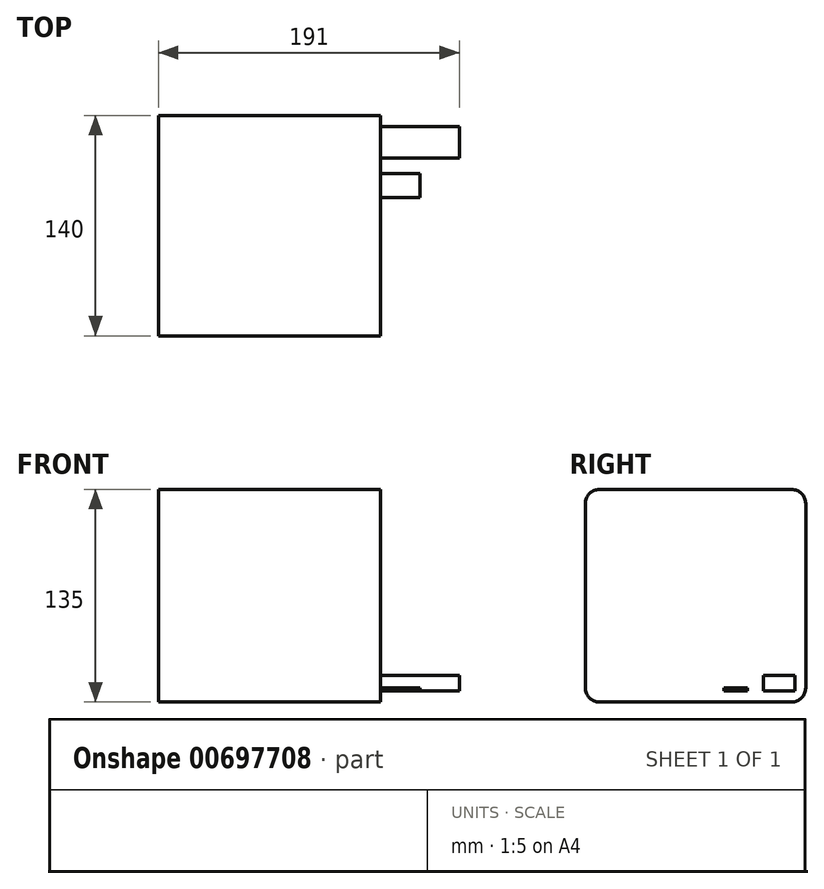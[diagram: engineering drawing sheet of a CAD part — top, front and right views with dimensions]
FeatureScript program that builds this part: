
annotation { "Feature Type Name" : "Feature", "Feature Type Description" : "" }
export const myFeature = defineFeature(function(context is Context, id is Id, definition is map)
    precondition{}
    {
        {
            var Q0;
            Q0=qCreatedBy(makeId("Top.planeOp"),FACE);
            var sketch = newSketch(context, id + "F0", { "sketchPlane" : qUnion([Q0])});
            skLineSegment(sketch, "E0.bottom", {"start": v(0, 0) * mm, "end": v(141, 0) * mm});
            skLineSegment(sketch, "E0.top", {"start": v(0, 140) * mm, "end": v(141, 140) * mm});
            skLineSegment(sketch, "E0.left", {"start": v(0, 0) * mm, "end": v(0, 140) * mm});
            skLineSegment(sketch, "E0.right", {"start": v(141, 0) * mm, "end": v(141, 140) * mm});
            skSolve(sketch);
        }
        {
            var Q0;
            Q0=makeQuery(id+"F0.imprint","IMPRINT",FACE,{"disambiguationData":[TD([[makeQuery(id+"F0.imprint","IMPRINT",EDGE,{"derivedFrom":sQuery(id+"F0.wireOp",EDGE,"E0.bottom")}),1.0]])]});
            extrude(context, id + "F1", {"entities" : qUnion([Q0]), "depth" : 135 * mm, "offsetDistance" : 25 * mm});
        }
        {
            var Q0;
            Q0=makeQuery(id+"F1.opExtrude","SWEPT_FACE",FACE,{"disambiguationData":[OSD([sQuery(id+"F0.wireOp",EDGE,"E0.right")])]});
            var sketch = newSketch(context, id + "F2", { "sketchPlane" : qUnion([Q0])});
            skLineSegment(sketch, "E1", {"start": v(140, 140) * mm, "end": v(140, 0) * mm});
            skLineSegment(sketch, "E2", {"start": v(0, 135) * mm, "end": v(150, 135) * mm});
            skLineSegment(sketch, "E3", {"start": v(0, 140) * mm, "end": v(0, 0) * mm});
            skLineSegment(sketch, "E4", {"start": v(0, 0) * mm, "end": v(150, 0) * mm});
            skLineSegment(sketch, "E5.bottom", {"start": v(103, 9) * mm, "end": v(88, 9) * mm});
            skLineSegment(sketch, "E5.top", {"start": v(103, 7) * mm, "end": v(88, 7) * mm});
            skLineSegment(sketch, "E5.left", {"start": v(103, 9) * mm, "end": v(103, 7) * mm});
            skLineSegment(sketch, "E5.right", {"start": v(88, 9) * mm, "end": v(88, 7) * mm});
            skLineSegment(sketch, "E6.bottom", {"start": v(133, 17) * mm, "end": v(113, 17) * mm});
            skLineSegment(sketch, "E6.top", {"start": v(133, 7) * mm, "end": v(113, 7) * mm});
            skLineSegment(sketch, "E6.left", {"start": v(133, 17) * mm, "end": v(133, 7) * mm});
            skLineSegment(sketch, "E6.right", {"start": v(113, 17) * mm, "end": v(113, 7) * mm});
            skSolve(sketch);
        }
        {
            var Q0;
            Q0=makeQuery(id+"F1.opExtrude","CAP_EDGE",EDGE,{"disambiguationData":[OSD([sQuery(id+"F0.wireOp",EDGE,"E0.top")])],"isStart":true});
            var Q1;
            Q1=makeQuery(id+"F1.opExtrude","CAP_EDGE",EDGE,{"disambiguationData":[OSD([sQuery(id+"F0.wireOp",EDGE,"E0.top")])],"isStart":false});
            var Q2;
            Q2=makeQuery(id+"F1.opExtrude","CAP_EDGE",EDGE,{"disambiguationData":[OSD([sQuery(id+"F0.wireOp",EDGE,"E0.bottom")])],"isStart":true});
            var Q3;
            Q3=makeQuery(id+"F1.opExtrude","CAP_EDGE",EDGE,{"disambiguationData":[OSD([sQuery(id+"F0.wireOp",EDGE,"E0.bottom")])],"isStart":false});
            fillet(context, id + "F3", {"entities" : qUnion([Q0, Q1, Q2, Q3]), "radius" : 9 * mm, "tangentPropagation" : true, "allowEdgeOverflow" : false});
        }
        {
            var Q0;
            Q0=makeQuery(id+"F2.imprint","IMPRINT",FACE,{"disambiguationData":[TD([[makeQuery(id+"F2.imprint","IMPRINT",EDGE,{"derivedFrom":sQuery(id+"F2.wireOp",EDGE,"E6.bottom")}),1.0]])]});
            extrude(context, id + "F4", {"entities" : qUnion([Q0]), "operationType" : NewBodyOperationType.ADD, "depth" : 50 * mm, "offsetDistance" : 25 * mm});
        }
        {
            var Q0;
            Q0=makeQuery(id+"F2.imprint","IMPRINT",FACE,{"disambiguationData":[TD([[makeQuery(id+"F2.imprint","IMPRINT",EDGE,{"derivedFrom":sQuery(id+"F2.wireOp",EDGE,"E5.bottom")}),1.0]])]});
            extrude(context, id + "F5", {"entities" : qUnion([Q0]), "operationType" : NewBodyOperationType.ADD, "depth" : 25 * mm, "offsetDistance" : 25 * mm});
        }
    });
